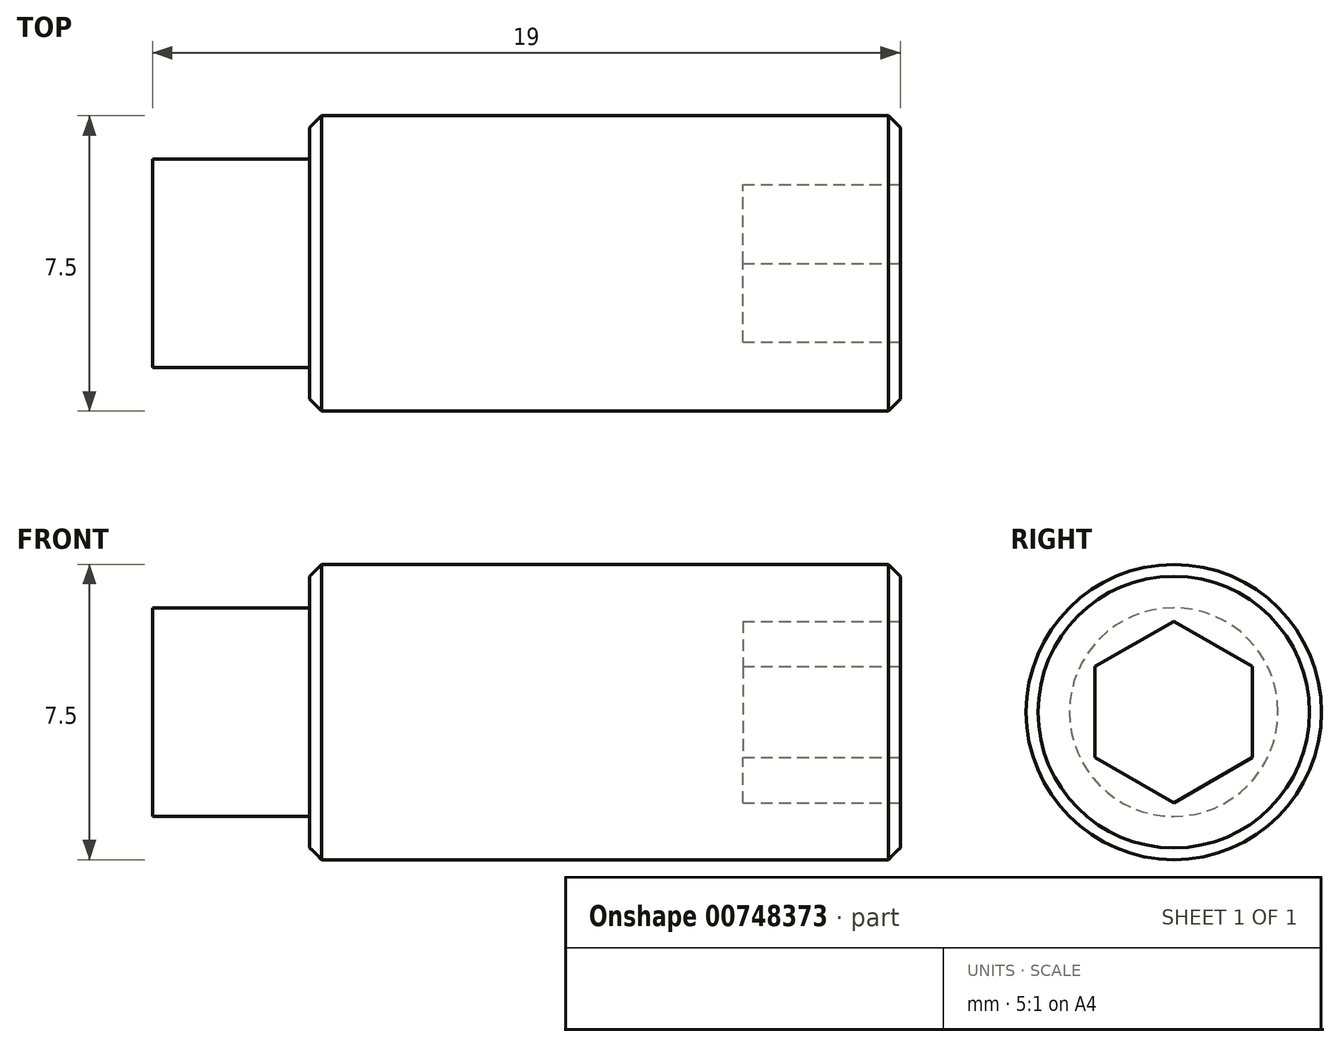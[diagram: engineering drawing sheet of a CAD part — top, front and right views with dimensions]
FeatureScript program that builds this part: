
annotation { "Feature Type Name" : "Feature", "Feature Type Description" : "" }
export const myFeature = defineFeature(function(context is Context, id is Id, definition is map)
    precondition{}
    {
        {
            var Q0;
            Q0=qCreatedBy(makeId("Right.planeOp"),FACE);
            var sketch = newSketch(context, id + "F0", { "sketchPlane" : qUnion([Q0])});
            skCircle(sketch, "E0", {"center": v(0, 0) * mm, "radius": 2.65 * mm});
            skSolve(sketch);
        }
        {
            var Q0;
            Q0 = qSketchRegion(id + "F0", true);
            extrude(context, id + "F1", {"entities" : qUnion([Q0]), "depth" : 4 * mm, "offsetDistance" : 25 * mm});
        }
        {
            var Q0;
            Q0=makeQuery(id+"F1.opExtrude","CAP_FACE",FACE,{"disambiguationData":[OSD([sQuery(id+"F0.wireOp",EDGE,"E0")])],"isStart":false});
            var sketch = newSketch(context, id + "F2", { "sketchPlane" : qUnion([Q0])});
            skCircle(sketch, "E1", {"center": v(0, 0) * mm, "radius": 3.75 * mm});
            skSolve(sketch);
        }
        {
            var Q0;
            Q0 = qSketchRegion(id + "F2", true);
            extrude(context, id + "F3", {"entities" : qUnion([Q0]), "operationType" : NewBodyOperationType.ADD, "depth" : 15 * mm, "offsetDistance" : 25 * mm});
        }
        {
            var Q0;
            Q0=makeQuery(id+"F3.opExtrude","CAP_FACE",FACE,{"disambiguationData":[OSD([sQuery(id+"F2.wireOp",EDGE,"E1")])],"isStart":false});
            var sketch = newSketch(context, id + "F4", { "sketchPlane" : qUnion([Q0])});
            skCircle(sketch, "E2.cCircle", {"center": v(0, 0) * mm, "radius": 2 * mm, "construction": true});
            skLineSegment(sketch, "E2.0", {"start": v(2, 1.15) * mm, "end": v(2, -1.15) * mm});
            skLineSegment(sketch, "E2.1", {"start": v(2, -1.15) * mm, "end": v(0, -2.3) * mm});
            skLineSegment(sketch, "E2.2", {"start": v(0, -2.3) * mm, "end": v(-2, -1.15) * mm});
            skLineSegment(sketch, "E2.3", {"start": v(-2, -1.15) * mm, "end": v(-2, 1.15) * mm});
            skLineSegment(sketch, "E2.4", {"start": v(-2, 1.15) * mm, "end": v(0, 2.3) * mm});
            skLineSegment(sketch, "E2.5", {"start": v(0, 2.3) * mm, "end": v(2, 1.15) * mm});
            skPoint(sketch, "E2.0.midPoint", {"position": v(2, 0) * mm});
            skSolve(sketch);
        }
        {
            var Q0;
            Q0 = qSketchRegion(id + "F4", true);
            extrude(context, id + "F5", {"entities" : qUnion([Q0]), "operationType" : NewBodyOperationType.REMOVE, "oppositeDirection" : true, "depth" : 4 * mm, "offsetDistance" : 25 * mm});
        }
        {
            var Q0;
            Q0=makeQuery(id+"F3.opExtrude","CAP_EDGE",EDGE,{"disambiguationData":[OSD([sQuery(id+"F2.wireOp",EDGE,"E1")])],"isStart":false});
            var Q1;
            Q1=makeQuery(id+"F3.opExtrude","CAP_EDGE",EDGE,{"disambiguationData":[OSD([sQuery(id+"F2.wireOp",EDGE,"E1")])],"isStart":true});
            chamfer(context, id + "F6", {"entities" : qUnion([Q0, Q1]), "width" : 0.3 * mm, "tangentPropagation" : true});
        }
    });
